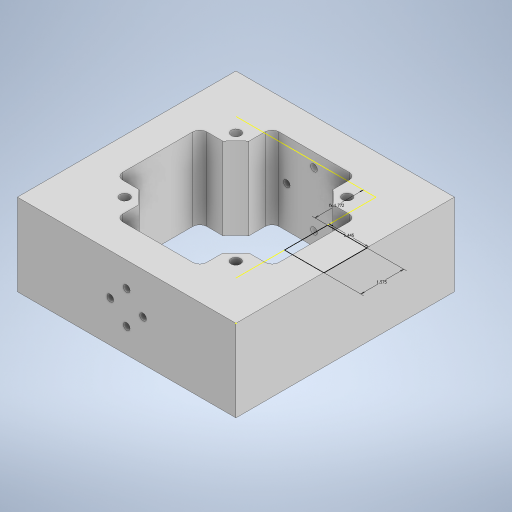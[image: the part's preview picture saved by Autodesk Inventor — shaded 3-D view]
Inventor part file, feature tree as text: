
AUTODESK INVENTOR PART (.ipt)
format: ipt  version: 2024 (Build 280153000, 153)  size: 381,440 bytes
history: native  units: in
note: dims shown in document units (in); Inventor stores cm internally (conversion verified against a paired STEP export)
features: sketch x8, extrude x7, fillet x1
ambient origin geometry x8: Origin, YZ Plane, XZ Plane, XY Plane, X Axis, Y Axis, Z Axis, Center Point
bodies: Body1 (feature_tree)
feature tree (16):
  extrude  "Extrusion15"  Depth=8.0in
  extrude  "Extrusion16"  Depth=3.0in
  extrude  "Extrusion17"  Depth=1.4409in
  sketch  "Sketch19"  dims[d156=1.4409in d157=0.0in d158=0.0in]
  sketch  "Sketch22"  dims[d159=4.0in d160=1.5in]
  extrude  "Extrusion20"  TaperAngle=0.0deg  [1 undecoded]
  extrude  "Extrusion28"  Depth=1.5in
  extrude  "Extrusion29"  Depth=0.25in
  extrude  "Extrusion30"  Depth=1.5748in TaperAngle=360.0deg
  fillet  "Fillet9"  Radius=4.0in
  sketch  "Sketch15"  dims[d149=8.0in d150=8.0in]
  sketch  "Sketch16"  dims[d151=3.0in d152=0.0in d153=5.1181in]
  sketch  "Sketch17"  dims[d154=5.1181in d155=1.4409in]
  sketch  "Sketch23"  dims[d161=0.25in d162=0.6in]
  sketch  "Sketch26"  dims[d163=0.0in d164=1.5748in d166=360.0deg d168=4.0in d169=0.0in]
  sketch  "Sketch28"  dims[d170=1.5748in d171=1.7717in d172=1.445in d180=4.0in d181=1.5in d182=1.0in d183=0.0in d184=0.25in d185=1.5748in d187=360.0deg d189=4.0in d190=0.0in d191=1.0236in d206=0.5467in d207=0.5467in d208=2.6in d209=1.0236in d210=0.5256in d214=0.354in d217=0.5026in d218=1.0236in d219=1.0236in d220=0.5467in d221=0.5467in d222=2.6in d223=0.354in d224=0.5026in d225=0.5256in d232=90.0deg d233=1.0236in d234=2.5591in d235=5.1181in d236=0.0in d237=3.0in d238=0.0in d242=0.0in d243=0.3in d244=0.0in d245=0.3in d246=0.0in d247=0.0in d253=0.0in d254=0.3in d255=0.0in d256=0.3in d257=0.0in d258=0.0in d259=0.25in d28=0.0in d29=0.0in d30=0.0in d31=0.0in d144=0.0197in d145=0.0344in d146=0.0197in d147=0.0344in d192=0.0344in d212=0.5in d213=0.0344in d215=0.0344in d260=0.5in d261=0.0344in d262=0.5in d263=0.0344in]
note: 1 required parameter value undecoded (feature->parameter linkage not recoverable at this tier; creation-order binding heuristic only, values carry confidence <= 0.55)
